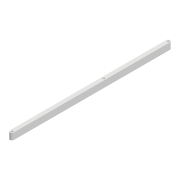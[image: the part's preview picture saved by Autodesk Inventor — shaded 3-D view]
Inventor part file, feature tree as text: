
AUTODESK INVENTOR PART (.ipt)
format: ipt  version: 2022 (Build 260153000, 153)  size: 88,576 bytes
history: native  units: mm
features: extrude x1, sketch x1
ambient origin geometry x8: Origin, YZ Plane, XZ Plane, XY Plane, X Axis, Y Axis, Z Axis, Center Point
bodies: Solid1 (feature_tree)
feature tree (2):
  extrude  "Extrusion1"  Depth=240.109mm
  sketch  "Sketch1"  dims[d0=6.0mm d1=240.109mm d2=3.0mm d3=3.0mm d4=10.0mm d5=0.0mm d6=3.0mm d7=141.04mm]
